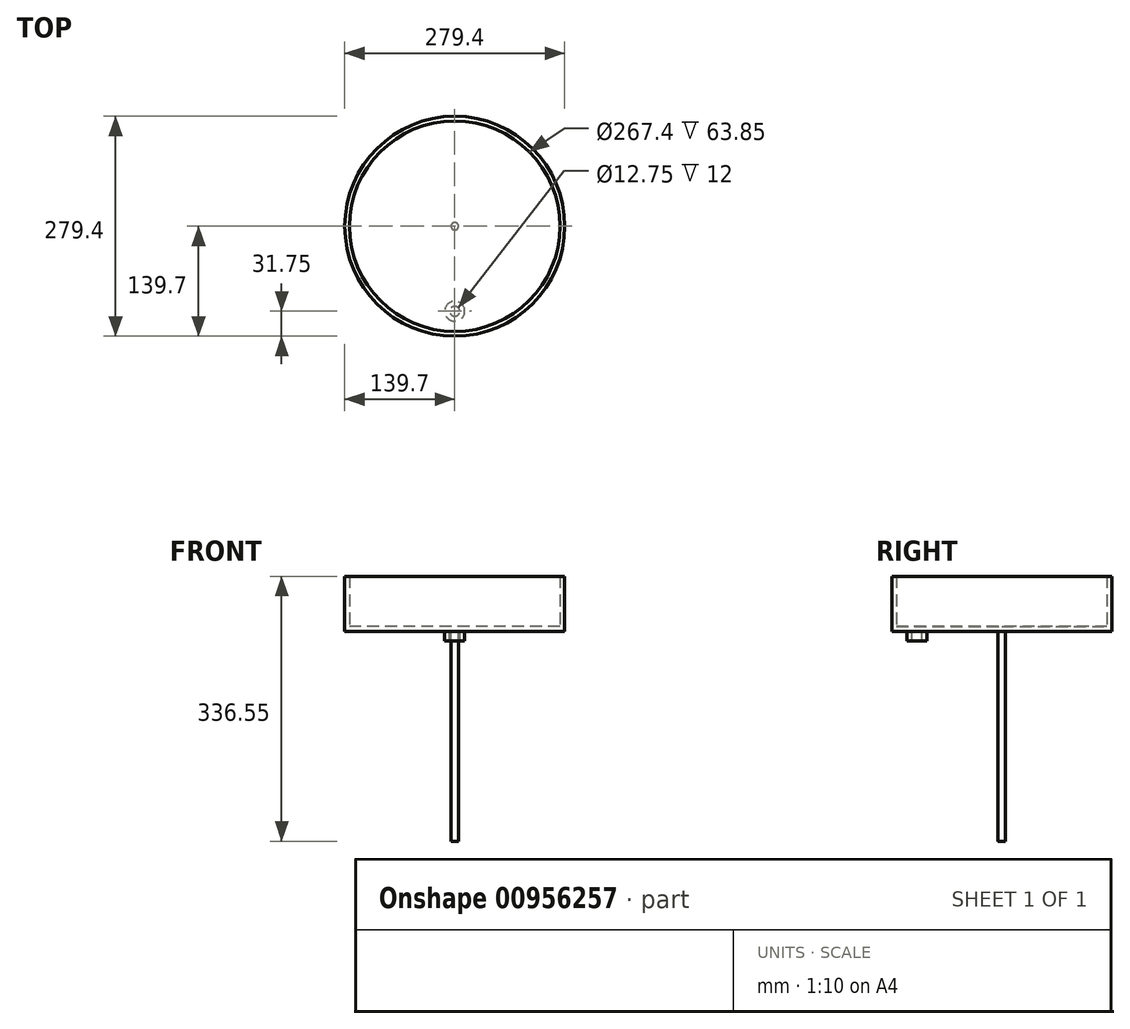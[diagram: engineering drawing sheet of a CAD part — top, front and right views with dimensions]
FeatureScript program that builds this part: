
annotation { "Feature Type Name" : "Feature", "Feature Type Description" : "" }
export const myFeature = defineFeature(function(context is Context, id is Id, definition is map)
    precondition{}
    {
        {
            var Q0;
            Q0=qCreatedBy(makeId("Top.planeOp"),FACE);
            var sketch = newSketch(context, id + "F0", { "sketchPlane" : qUnion([Q0])});
            skCircle(sketch, "E0", {"center": v(0, 0) * mm, "radius": 139.7 * mm});
            skSolve(sketch);
        }
        {
            var Q0;
            Q0 = qSketchRegion(id + "F0", true);
            extrude(context, id + "F1", {"entities" : qUnion([Q0]), "depth" : 69.85 * mm, "offsetDistance" : 25 * mm});
        }
        {
            var Q0;
            Q0=makeQuery(id+"F1.opExtrude","CAP_FACE",FACE,{"disambiguationData":[OSD([sQuery(id+"F0.wireOp",EDGE,"E0")])],"isStart":false});
            shell(context, id + "F2", {"entities" : qUnion([Q0]), "thickness" : 6 * mm});
        }
        {
            var Q0;
            Q0=makeQuery(id+"F1.opExtrude","CAP_FACE",FACE,{"disambiguationData":[OSD([sQuery(id+"F0.wireOp",EDGE,"E0")])],"isStart":true});
            var sketch = newSketch(context, id + "F3", { "sketchPlane" : qUnion([Q0])});
            skCircle(sketch, "E1", {"center": v(0, 107.95) * mm, "radius": 12.7 * mm});
            skCircle(sketch, "E2", {"center": v(0, 107.95) * mm, "radius": 6.38 * mm});
            skSolve(sketch);
        }
        {
            var Q0;
            Q0=makeQuery(id+"F3.imprint","IMPRINT",FACE,{"disambiguationData":[TD([[makeQuery(id+"F3.imprint","IMPRINT",EDGE,{"derivedFrom":sQuery(id+"F3.wireOp",EDGE,"E1")}),1.0]])]});
            extrude(context, id + "F4", {"entities" : qUnion([Q0]), "operationType" : NewBodyOperationType.ADD, "depth" : 12 * mm, "offsetDistance" : 25 * mm});
        }
        {
            var Q0;
            Q0=qCreatedBy(makeId("Front.planeOp"),FACE);
            var sketch = newSketch(context, id + "F5", { "sketchPlane" : qUnion([Q0])});
            skLineSegment(sketch, "E3", {"start": v(0, 0) * mm, "end": v(0, -183.16) * mm, "construction": true});
            skSolve(sketch);
        }
        {
            var Q0;
            {var subQ4=sQuery(id+"F0.wireOp",EDGE,"E0");var subQ5=makeQuery(id+"F1.opExtrude","SWEPT_FACE",FACE,{"disambiguationData":[OSD([subQ4])]});Q0=makeQuery(id+"FfkUhh9lbX5U9Uw_1.4.F4.boolean.opBoolean","SPLIT",FACE,{"disambiguationData":[TD([subQ5])],"derivedFrom":makeQuery(id+"FfkUhh9lbX5U9Uw_1.3.F4.boolean.opBoolean","SPLIT",FACE,{"disambiguationData":[TD([subQ5])],"derivedFrom":makeQuery(id+"FfkUhh9lbX5U9Uw_1.2.F4.boolean.opBoolean","SPLIT",FACE,{"disambiguationData":[TD([subQ5])],"derivedFrom":makeQuery(id+"FfkUhh9lbX5U9Uw_1.1.F4.boolean.opBoolean","SPLIT",FACE,{"disambiguationData":[TD([subQ5])],"derivedFrom":makeQuery(id+"F4.boolean.opBoolean","SPLIT",FACE,{"disambiguationData":[TD([subQ5])],"derivedFrom":makeQuery(id+"F1.opExtrude","CAP_FACE",FACE,{"disambiguationData":[OSD([subQ4])],"isStart":true})})})})})});}
            var sketch = newSketch(context, id + "F6", { "sketchPlane" : qUnion([Q0])});
            skCircle(sketch, "E4", {"center": v(0, 0) * mm, "radius": 4.76 * mm});
            skSolve(sketch);
        }
        {
            var Q0;
            Q0 = qSketchRegion(id + "F6", true);
            extrude(context, id + "F7", {"entities" : qUnion([Q0]), "operationType" : NewBodyOperationType.ADD, "depth" : 266.7 * mm, "offsetDistance" : 25 * mm});
        }
    });
